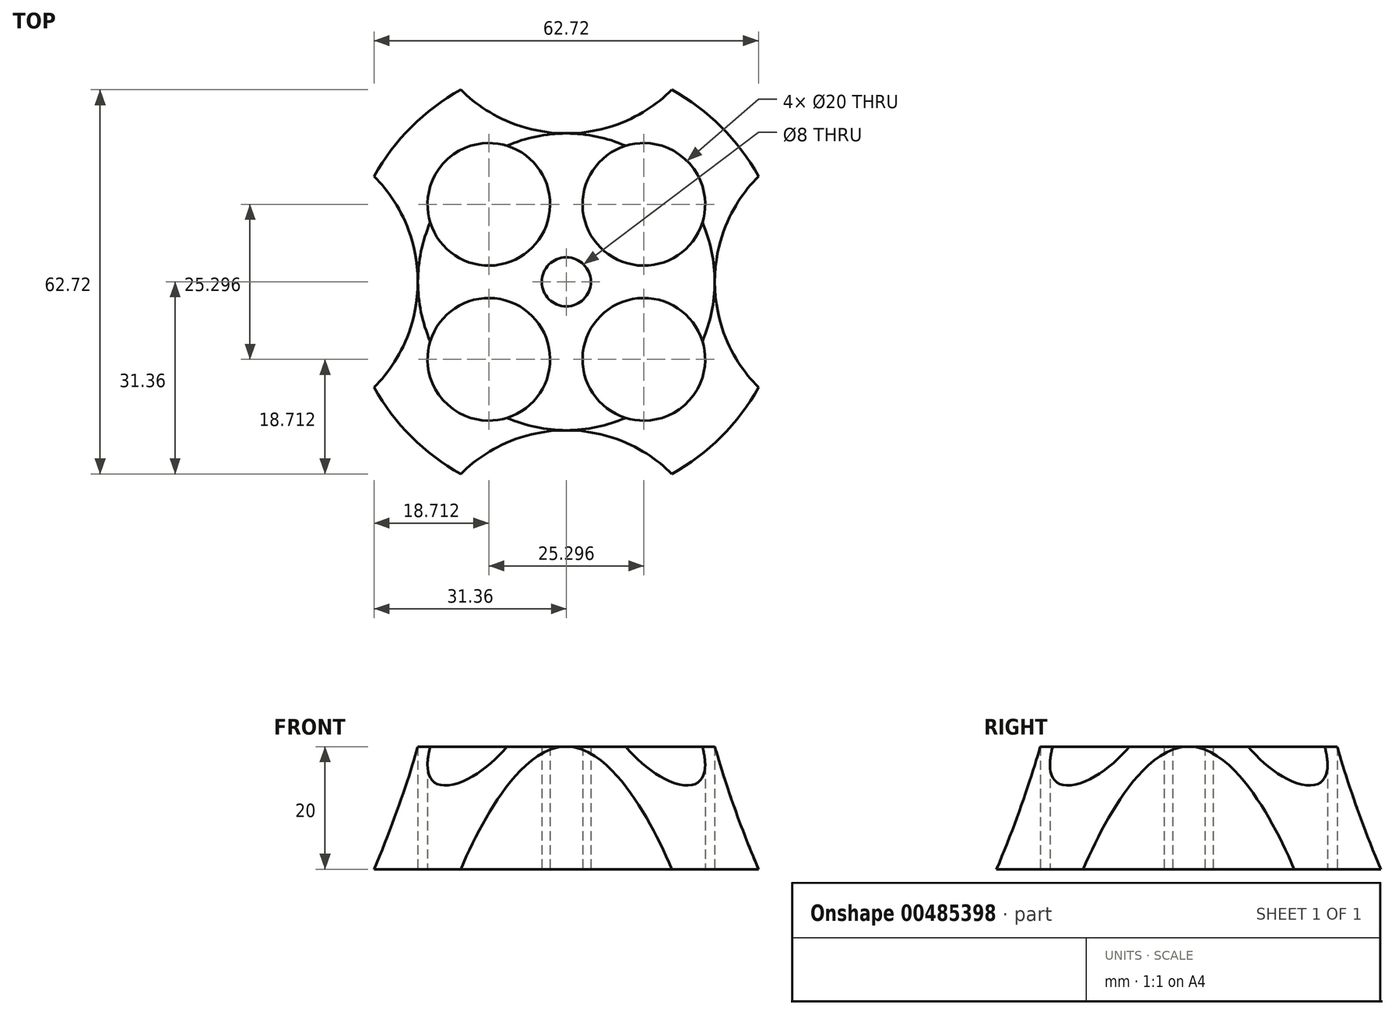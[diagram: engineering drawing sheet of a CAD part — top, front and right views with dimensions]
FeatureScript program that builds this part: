
annotation { "Feature Type Name" : "Feature", "Feature Type Description" : "" }
export const myFeature = defineFeature(function(context is Context, id is Id, definition is map)
    precondition{}
    {
        {
            var Q0;
            Q0=qCreatedBy(makeId("Front.planeOp"),FACE);
            var sketch = newSketch(context, id + "F0", { "sketchPlane" : qUnion([Q0])});
            skLineSegment(sketch, "E0", {"start": v(0, 0) * mm, "end": v(0, 20) * mm, "construction": true});
            skLineSegment(sketch, "E1", {"start": v(0, 20) * mm, "end": v(-24.23, 20) * mm});
            skLineSegment(sketch, "E2", {"start": v(-24.23, 20) * mm, "end": v(-35.77, 0) * mm});
            skLineSegment(sketch, "E3", {"start": v(-35.77, 0) * mm, "end": v(0, 0) * mm});
            skLineSegment(sketch, "E4", {"start": v(0, 10) * mm, "end": v(-30, 10) * mm, "construction": true});
            skLineSegment(sketch, "E5", {"start": v(-4, 20) * mm, "end": v(-4, 0) * mm});
            skSolve(sketch);
        }
        {
            var Q0;
            {var subQ0=sQuery(id+"F0.wireOp",EDGE,"E2");Q0=makeQuery(id+"F0.imprint","IMPRINT",FACE,{"disambiguationData":[TD([[makeQuery(id+"F0.imprint","IMPRINT",EDGE,{"derivedFrom":subQ0}),1.0]])]});}
            var Q1;
            Q1=sQuery(id+"F0.wireOp",EDGE,"E0");
            revolve(context, id + "F1", {"entities" : qUnion([Q0]), "axis" : qUnion([Q1]), "revolveType" : RevolveType.FULL});
        }
        {
            var Q0;
            Q0=qCreatedBy(makeId("Top.planeOp"),FACE);
            var sketch = newSketch(context, id + "F2", { "sketchPlane" : qUnion([Q0])});
            skCircle(sketch, "E6.0", {"center": v(0, 0) * mm, "radius": 35.77 * mm});
            skArc(sketch, "E7", {"start": v(-31.36, -17.22) * mm, "mid": v(-24.23, 0) * mm, "end": v(-31.36, 17.22) * mm});
            skLineSegment(sketch, "E8", {"start": v(-31.36, 17.22) * mm, "end": v(-14.14, 0) * mm, "construction": true});
            skLineSegment(sketch, "E9", {"start": v(-14.14, 0) * mm, "end": v(0, 0) * mm, "construction": true});
            skArc(sketch, "E10.1.0", {"start": v(17.22, -31.36) * mm, "mid": v(0, -24.23) * mm, "end": v(-17.22, -31.36) * mm});
            skArc(sketch, "E10.2.0", {"start": v(31.36, 17.22) * mm, "mid": v(24.23, 0) * mm, "end": v(31.36, -17.22) * mm});
            skArc(sketch, "E10.3.0", {"start": v(-17.22, 31.36) * mm, "mid": v(0, 24.23) * mm, "end": v(17.22, 31.36) * mm});
            skSolve(sketch);
        }
        {
            var Q0;
            {var subQ0=sQuery(id+"F2.wireOp",EDGE,"E10.3.0");Q0=makeQuery(id+"F2.imprint","IMPRINT",FACE,{"disambiguationData":[TD([[makeQuery(id+"F2.imprint","IMPRINT",EDGE,{"derivedFrom":subQ0}),1.0]])]});}
            var Q1;
            {var subQ0=sQuery(id+"F2.wireOp",EDGE,"E10.2.0");Q1=makeQuery(id+"F2.imprint","IMPRINT",FACE,{"disambiguationData":[TD([[makeQuery(id+"F2.imprint","IMPRINT",EDGE,{"derivedFrom":subQ0}),1.0]])]});}
            var Q2;
            {var subQ0=sQuery(id+"F2.wireOp",EDGE,"E10.1.0");Q2=makeQuery(id+"F2.imprint","IMPRINT",FACE,{"disambiguationData":[TD([[makeQuery(id+"F2.imprint","IMPRINT",EDGE,{"derivedFrom":subQ0}),1.0]])]});}
            var Q3;
            {var subQ0=sQuery(id+"F2.wireOp",EDGE,"E7");Q3=makeQuery(id+"F2.imprint","IMPRINT",FACE,{"disambiguationData":[TD([[makeQuery(id+"F2.imprint","IMPRINT",EDGE,{"derivedFrom":subQ0}),1.0]])]});}
            extrude(context, id + "F3", {"entities" : qUnion([Q0, Q1, Q2, Q3]), "operationType" : NewBodyOperationType.REMOVE, "endBound" : BoundingType.THROUGH_ALL, "depth" : 25 * mm});
        }
        {
            var Q0;
            Q0=qCreatedBy(makeId("Top.planeOp"),FACE);
            var sketch = newSketch(context, id + "F4", { "sketchPlane" : qUnion([Q0])});
            skCircle(sketch, "E11", {"center": v(-12.65, -12.65) * mm, "radius": 10 * mm});
            skCircle(sketch, "E12", {"center": v(12.65, -12.65) * mm, "radius": 10 * mm});
            skCircle(sketch, "E13", {"center": v(12.65, 12.65) * mm, "radius": 10 * mm});
            skCircle(sketch, "E14", {"center": v(-12.65, 12.65) * mm, "radius": 10 * mm});
            skLineSegment(sketch, "E15.bottom", {"start": v(-12.65, 12.65) * mm, "end": v(12.65, 12.65) * mm, "construction": true});
            skLineSegment(sketch, "E15.top", {"start": v(-12.65, -12.65) * mm, "end": v(12.65, -12.65) * mm, "construction": true});
            skLineSegment(sketch, "E15.left", {"start": v(-12.65, 12.65) * mm, "end": v(-12.65, -12.65) * mm, "construction": true});
            skLineSegment(sketch, "E15.right", {"start": v(12.65, 12.65) * mm, "end": v(12.65, -12.65) * mm, "construction": true});
            skPoint(sketch, "E15.middle", {"position": v(0, 0) * mm});
            skLineSegment(sketch, "E16", {"start": v(-12.65, 12.65) * mm, "end": v(-25.3, 25.3) * mm, "construction": true});
            skLineSegment(sketch, "E17", {"start": v(-12.65, 12.65) * mm, "end": v(0, 0) * mm, "construction": true});
            skSolve(sketch);
        }
        {
            var Q0;
            Q0 = qSketchRegion(id + "F4", true);
            extrude(context, id + "F5", {"entities" : qUnion([Q0]), "operationType" : NewBodyOperationType.REMOVE, "endBound" : BoundingType.THROUGH_ALL, "depth" : 25 * mm});
        }
    });
